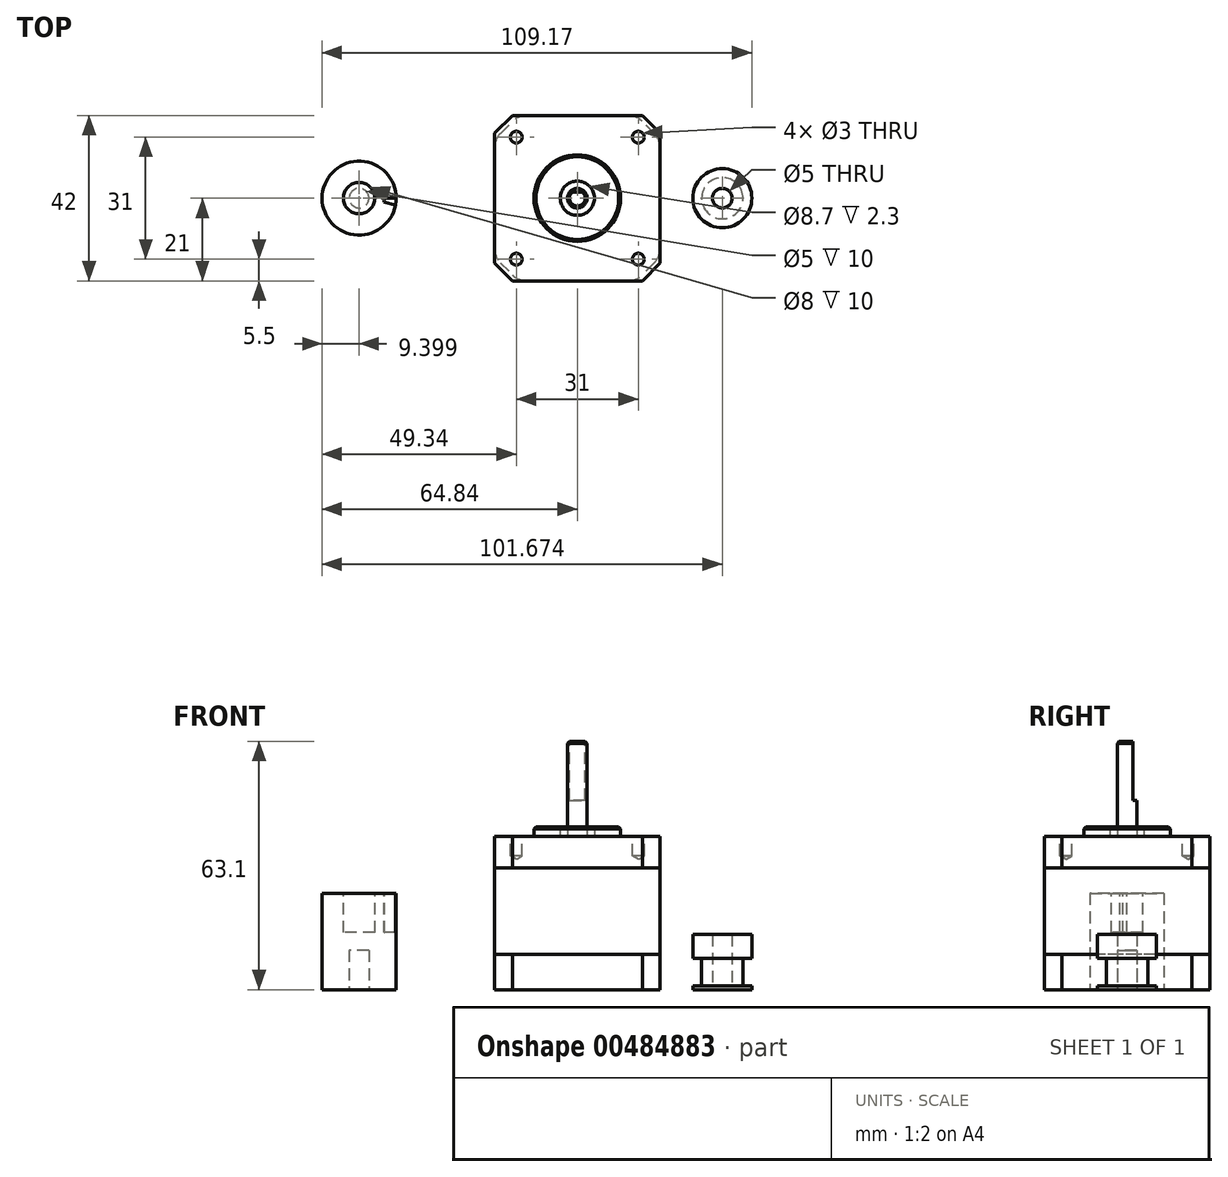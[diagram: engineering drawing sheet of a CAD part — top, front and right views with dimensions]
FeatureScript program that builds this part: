
annotation { "Feature Type Name" : "Feature", "Feature Type Description" : "" }
export const myFeature = defineFeature(function(context is Context, id is Id, definition is map)
    precondition{}
    {
        {
            var Q0;
            Q0=qCreatedBy(makeId("Top.planeOp"),FACE);
            var sketch = newSketch(context, id + "F0", { "sketchPlane" : qUnion([Q0])});
            skLineSegment(sketch, "E0.bottom", {"start": v(21, 21) * mm, "end": v(-21, 21) * mm});
            skLineSegment(sketch, "E0.top", {"start": v(21, -21) * mm, "end": v(-21, -21) * mm});
            skLineSegment(sketch, "E0.left", {"start": v(21, 21) * mm, "end": v(21, -21) * mm});
            skLineSegment(sketch, "E0.right", {"start": v(-21, 21) * mm, "end": v(-21, -21) * mm});
            skPoint(sketch, "E0.middle", {"position": v(0, 0) * mm});
            skSolve(sketch);
        }
        {
            var Q0;
            Q0=makeQuery(id+"F0.imprint","IMPRINT",FACE,{"disambiguationData":[TD([[makeQuery(id+"F0.imprint","IMPRINT",EDGE,{"derivedFrom":sQuery(id+"F0.wireOp",EDGE,"E0.bottom")}),1.0]])]});
            extrude(context, id + "F1", {"entities" : qUnion([Q0]), "depth" : 9 * mm, "offsetDistance" : 25 * mm});
        }
        {
            var Q0;
            Q0=makeQuery(id+"F1.opExtrude","SWEPT_EDGE",EDGE,{"disambiguationData":[OSD([sQuery(id+"F0.wireOp",EDGE,"E0.top"),sQuery(id+"F0.wireOp",EDGE,"E0.right")])]});
            var Q1;
            Q1=makeQuery(id+"F1.opExtrude","SWEPT_EDGE",EDGE,{"disambiguationData":[OSD([sQuery(id+"F0.wireOp",EDGE,"E0.top"),sQuery(id+"F0.wireOp",EDGE,"E0.left")])]});
            var Q2;
            Q2=makeQuery(id+"F1.opExtrude","SWEPT_EDGE",EDGE,{"disambiguationData":[OSD([sQuery(id+"F0.wireOp",EDGE,"E0.bottom"),sQuery(id+"F0.wireOp",EDGE,"E0.right")])]});
            var Q3;
            Q3=makeQuery(id+"F1.opExtrude","SWEPT_EDGE",EDGE,{"disambiguationData":[OSD([sQuery(id+"F0.wireOp",EDGE,"E0.bottom"),sQuery(id+"F0.wireOp",EDGE,"E0.left")])]});
            chamfer(context, id + "F2", {"entities" : qUnion([Q0, Q1, Q2, Q3]), "width" : 4.5 * mm, "tangentPropagation" : true});
        }
        {
            var Q0;
            Q0=makeQuery(id+"F1.opExtrude","CAP_FACE",FACE,{"disambiguationData":[OSD([sQuery(id+"F0.wireOp",EDGE,"E0.bottom"),sQuery(id+"F0.wireOp",EDGE,"E0.top"),sQuery(id+"F0.wireOp",EDGE,"E0.left"),sQuery(id+"F0.wireOp",EDGE,"E0.right")])],"isStart":false});
            var sketch = newSketch(context, id + "F3", { "sketchPlane" : qUnion([Q0])});
            skLineSegment(sketch, "E1.bottom", {"start": v(21, 21) * mm, "end": v(-21, 21) * mm});
            skLineSegment(sketch, "E1.top", {"start": v(21, -21) * mm, "end": v(-21, -21) * mm});
            skLineSegment(sketch, "E1.left", {"start": v(21, 21) * mm, "end": v(21, -21) * mm});
            skLineSegment(sketch, "E1.right", {"start": v(-21, 21) * mm, "end": v(-21, -21) * mm});
            skPoint(sketch, "E1.middle", {"position": v(0, 0) * mm});
            skSolve(sketch);
        }
        {
            var Q0;
            {var subQ1=sQuery(id+"F0.wireOp",EDGE,"E0.right");var subQ2=sQuery(id+"F0.wireOp",EDGE,"E0.left");var subQ3=sQuery(id+"F0.wireOp",EDGE,"E0.top");var subQ4=sQuery(id+"F0.wireOp",EDGE,"E0.bottom");var subQ5=makeQuery(id+"F1.opExtrude","CAP_FACE",FACE,{"disambiguationData":[OSD([subQ4,subQ3,subQ2,subQ1])],"isStart":false});var subQ9=makeQuery(id+"F2.opChamfer","BLEND_EDGE",EDGE,{"blendedFrom":[makeQuery(id+"F1.opExtrude","SWEPT_EDGE",EDGE,{"disambiguationData":[OSD([subQ4,subQ2])]}),subQ5],"blendedInto":[subQ5]});Q0=makeQuery(id+"F3.imprint","IMPRINT",FACE,{"disambiguationData":[TD([[makeQuery(id+"F3.imprint","IMPRINT",EDGE,{"derivedFrom":subQ9}),1.0]])]});}
            var Q1;
            {var subQ1=sQuery(id+"F0.wireOp",EDGE,"E0.right");var subQ2=sQuery(id+"F0.wireOp",EDGE,"E0.bottom");var subQ3=makeQuery(id+"F2.opChamfer","BLEND_EDGE",EDGE,{"blendedFrom":[makeQuery(id+"F1.opExtrude","SWEPT_EDGE",EDGE,{"disambiguationData":[OSD([subQ2,subQ1])]}),makeQuery(id+"F1.opExtrude","CAP_FACE",FACE,{"disambiguationData":[OSD([subQ2,sQuery(id+"F0.wireOp",EDGE,"E0.top"),sQuery(id+"F0.wireOp",EDGE,"E0.left"),subQ1])],"isStart":false})],"blendedInto":[makeQuery(id+"F1.opExtrude","CAP_FACE",FACE,{"disambiguationData":[OSD([subQ2,sQuery(id+"F0.wireOp",EDGE,"E0.top"),sQuery(id+"F0.wireOp",EDGE,"E0.left"),subQ1])],"isStart":false})]});Q1=makeQuery(id+"F3.imprint","IMPRINT",FACE,{"disambiguationData":[TD([[makeQuery(id+"F3.imprint","IMPRINT",EDGE,{"derivedFrom":subQ3}),-1.0]])]});}
            var Q2;
            {var subQ1=sQuery(id+"F0.wireOp",EDGE,"E0.left");var subQ2=sQuery(id+"F0.wireOp",EDGE,"E0.bottom");var subQ3=makeQuery(id+"F2.opChamfer","BLEND_EDGE",EDGE,{"blendedFrom":[makeQuery(id+"F1.opExtrude","SWEPT_EDGE",EDGE,{"disambiguationData":[OSD([subQ2,subQ1])]}),makeQuery(id+"F1.opExtrude","CAP_FACE",FACE,{"disambiguationData":[OSD([subQ2,sQuery(id+"F0.wireOp",EDGE,"E0.top"),subQ1,sQuery(id+"F0.wireOp",EDGE,"E0.right")])],"isStart":false})],"blendedInto":[makeQuery(id+"F1.opExtrude","CAP_FACE",FACE,{"disambiguationData":[OSD([subQ2,sQuery(id+"F0.wireOp",EDGE,"E0.top"),subQ1,sQuery(id+"F0.wireOp",EDGE,"E0.right")])],"isStart":false})]});Q2=makeQuery(id+"F3.imprint","IMPRINT",FACE,{"disambiguationData":[TD([[makeQuery(id+"F3.imprint","IMPRINT",EDGE,{"derivedFrom":subQ3}),-1.0]])]});}
            var Q3;
            {var subQ1=sQuery(id+"F0.wireOp",EDGE,"E0.right");var subQ2=sQuery(id+"F0.wireOp",EDGE,"E0.top");var subQ3=makeQuery(id+"F2.opChamfer","BLEND_EDGE",EDGE,{"blendedFrom":[makeQuery(id+"F1.opExtrude","SWEPT_EDGE",EDGE,{"disambiguationData":[OSD([subQ2,subQ1])]}),makeQuery(id+"F1.opExtrude","CAP_FACE",FACE,{"disambiguationData":[OSD([sQuery(id+"F0.wireOp",EDGE,"E0.bottom"),subQ2,sQuery(id+"F0.wireOp",EDGE,"E0.left"),subQ1])],"isStart":false})],"blendedInto":[makeQuery(id+"F1.opExtrude","CAP_FACE",FACE,{"disambiguationData":[OSD([sQuery(id+"F0.wireOp",EDGE,"E0.bottom"),subQ2,sQuery(id+"F0.wireOp",EDGE,"E0.left"),subQ1])],"isStart":false})]});Q3=makeQuery(id+"F3.imprint","IMPRINT",FACE,{"disambiguationData":[TD([[makeQuery(id+"F3.imprint","IMPRINT",EDGE,{"derivedFrom":subQ3}),-1.0]])]});}
            var Q4;
            {var subQ1=sQuery(id+"F0.wireOp",EDGE,"E0.left");var subQ2=sQuery(id+"F0.wireOp",EDGE,"E0.top");var subQ3=makeQuery(id+"F2.opChamfer","BLEND_EDGE",EDGE,{"blendedFrom":[makeQuery(id+"F1.opExtrude","SWEPT_EDGE",EDGE,{"disambiguationData":[OSD([subQ2,subQ1])]}),makeQuery(id+"F1.opExtrude","CAP_FACE",FACE,{"disambiguationData":[OSD([sQuery(id+"F0.wireOp",EDGE,"E0.bottom"),subQ2,subQ1,sQuery(id+"F0.wireOp",EDGE,"E0.right")])],"isStart":false})],"blendedInto":[makeQuery(id+"F1.opExtrude","CAP_FACE",FACE,{"disambiguationData":[OSD([sQuery(id+"F0.wireOp",EDGE,"E0.bottom"),subQ2,subQ1,sQuery(id+"F0.wireOp",EDGE,"E0.right")])],"isStart":false})]});Q4=makeQuery(id+"F3.imprint","IMPRINT",FACE,{"disambiguationData":[TD([[makeQuery(id+"F3.imprint","IMPRINT",EDGE,{"derivedFrom":subQ3}),-1.0]])]});}
            extrude(context, id + "F4", {"entities" : qUnion([Q0, Q1, Q2, Q3, Q4]), "depth" : 22 * mm, "offsetDistance" : 25 * mm});
        }
        {
            var Q0;
            Q0=makeQuery(id+"F4.opExtrude","SWEPT_EDGE",EDGE,{"disambiguationData":[OSD([sQuery(id+"F3.wireOp",EDGE,"E1.bottom"),sQuery(id+"F3.wireOp",EDGE,"E1.right")])]});
            var Q1;
            Q1=makeQuery(id+"F4.opExtrude","SWEPT_EDGE",EDGE,{"disambiguationData":[OSD([sQuery(id+"F3.wireOp",EDGE,"E1.top"),sQuery(id+"F3.wireOp",EDGE,"E1.right")])]});
            var Q2;
            Q2=makeQuery(id+"F4.opExtrude","SWEPT_EDGE",EDGE,{"disambiguationData":[OSD([sQuery(id+"F3.wireOp",EDGE,"E1.bottom"),sQuery(id+"F3.wireOp",EDGE,"E1.left")])]});
            var Q3;
            Q3=makeQuery(id+"F4.opExtrude","SWEPT_EDGE",EDGE,{"disambiguationData":[OSD([sQuery(id+"F3.wireOp",EDGE,"E1.top"),sQuery(id+"F3.wireOp",EDGE,"E1.left")])]});
            chamfer(context, id + "F5", {"entities" : qUnion([Q0, Q1, Q2, Q3]), "width" : 6 * mm, "tangentPropagation" : true});
        }
        {
            var Q0;
            {var subQ0=sQuery(id+"F3.wireOp",EDGE,"E1.bottom");Q0=makeQuery(id+"F5.opChamfer","BLEND_EDGE",EDGE,{"blendedFrom":[makeQuery(id+"F4.opExtrude","SWEPT_EDGE",EDGE,{"disambiguationData":[OSD([subQ0,sQuery(id+"F3.wireOp",EDGE,"E1.right")])]}),makeQuery(id+"F4.opExtrude","SWEPT_FACE",FACE,{"disambiguationData":[OSD([subQ0])]})],"blendedInto":[makeQuery(id+"F4.opExtrude","SWEPT_FACE",FACE,{"disambiguationData":[OSD([subQ0])]})]});}
            var Q1;
            {var subQ0=sQuery(id+"F3.wireOp",EDGE,"E1.right");Q1=makeQuery(id+"F5.opChamfer","BLEND_EDGE",EDGE,{"blendedFrom":[makeQuery(id+"F4.opExtrude","SWEPT_EDGE",EDGE,{"disambiguationData":[OSD([sQuery(id+"F3.wireOp",EDGE,"E1.bottom"),subQ0])]}),makeQuery(id+"F4.opExtrude","SWEPT_FACE",FACE,{"disambiguationData":[OSD([subQ0])]})],"blendedInto":[makeQuery(id+"F4.opExtrude","SWEPT_FACE",FACE,{"disambiguationData":[OSD([subQ0])]})]});}
            var Q2;
            {var subQ0=sQuery(id+"F3.wireOp",EDGE,"E1.right");Q2=makeQuery(id+"F5.opChamfer","BLEND_EDGE",EDGE,{"blendedFrom":[makeQuery(id+"F4.opExtrude","SWEPT_EDGE",EDGE,{"disambiguationData":[OSD([sQuery(id+"F3.wireOp",EDGE,"E1.top"),subQ0])]}),makeQuery(id+"F4.opExtrude","SWEPT_FACE",FACE,{"disambiguationData":[OSD([subQ0])]})],"blendedInto":[makeQuery(id+"F4.opExtrude","SWEPT_FACE",FACE,{"disambiguationData":[OSD([subQ0])]})]});}
            var Q3;
            {var subQ0=sQuery(id+"F3.wireOp",EDGE,"E1.top");Q3=makeQuery(id+"F5.opChamfer","BLEND_EDGE",EDGE,{"blendedFrom":[makeQuery(id+"F4.opExtrude","SWEPT_EDGE",EDGE,{"disambiguationData":[OSD([subQ0,sQuery(id+"F3.wireOp",EDGE,"E1.right")])]}),makeQuery(id+"F4.opExtrude","SWEPT_FACE",FACE,{"disambiguationData":[OSD([subQ0])]})],"blendedInto":[makeQuery(id+"F4.opExtrude","SWEPT_FACE",FACE,{"disambiguationData":[OSD([subQ0])]})]});}
            var Q4;
            {var subQ0=sQuery(id+"F3.wireOp",EDGE,"E1.top");Q4=makeQuery(id+"F5.opChamfer","BLEND_EDGE",EDGE,{"blendedFrom":[makeQuery(id+"F4.opExtrude","SWEPT_EDGE",EDGE,{"disambiguationData":[OSD([subQ0,sQuery(id+"F3.wireOp",EDGE,"E1.left")])]}),makeQuery(id+"F4.opExtrude","SWEPT_FACE",FACE,{"disambiguationData":[OSD([subQ0])]})],"blendedInto":[makeQuery(id+"F4.opExtrude","SWEPT_FACE",FACE,{"disambiguationData":[OSD([subQ0])]})]});}
            var Q5;
            {var subQ0=sQuery(id+"F3.wireOp",EDGE,"E1.left");Q5=makeQuery(id+"F5.opChamfer","BLEND_EDGE",EDGE,{"blendedFrom":[makeQuery(id+"F4.opExtrude","SWEPT_EDGE",EDGE,{"disambiguationData":[OSD([sQuery(id+"F3.wireOp",EDGE,"E1.top"),subQ0])]}),makeQuery(id+"F4.opExtrude","SWEPT_FACE",FACE,{"disambiguationData":[OSD([subQ0])]})],"blendedInto":[makeQuery(id+"F4.opExtrude","SWEPT_FACE",FACE,{"disambiguationData":[OSD([subQ0])]})]});}
            var Q6;
            {var subQ0=sQuery(id+"F3.wireOp",EDGE,"E1.left");Q6=makeQuery(id+"F5.opChamfer","BLEND_EDGE",EDGE,{"blendedFrom":[makeQuery(id+"F4.opExtrude","SWEPT_EDGE",EDGE,{"disambiguationData":[OSD([sQuery(id+"F3.wireOp",EDGE,"E1.bottom"),subQ0])]}),makeQuery(id+"F4.opExtrude","SWEPT_FACE",FACE,{"disambiguationData":[OSD([subQ0])]})],"blendedInto":[makeQuery(id+"F4.opExtrude","SWEPT_FACE",FACE,{"disambiguationData":[OSD([subQ0])]})]});}
            var Q7;
            {var subQ0=sQuery(id+"F3.wireOp",EDGE,"E1.bottom");Q7=makeQuery(id+"F5.opChamfer","BLEND_EDGE",EDGE,{"blendedFrom":[makeQuery(id+"F4.opExtrude","SWEPT_EDGE",EDGE,{"disambiguationData":[OSD([subQ0,sQuery(id+"F3.wireOp",EDGE,"E1.left")])]}),makeQuery(id+"F4.opExtrude","SWEPT_FACE",FACE,{"disambiguationData":[OSD([subQ0])]})],"blendedInto":[makeQuery(id+"F4.opExtrude","SWEPT_FACE",FACE,{"disambiguationData":[OSD([subQ0])]})]});}
            fillet(context, id + "F6", {"entities" : qUnion([Q0, Q1, Q2, Q3, Q4, Q5, Q6, Q7]), "radius" : 5 * mm, "tangentPropagation" : true, "allowEdgeOverflow" : false});
        }
        {
            var Q0;
            Q0=makeQuery(id+"F4.opExtrude","CAP_FACE",FACE,{"disambiguationData":[OSD([sQuery(id+"F3.wireOp",EDGE,"E1.bottom"),sQuery(id+"F3.wireOp",EDGE,"E1.top"),sQuery(id+"F3.wireOp",EDGE,"E1.left"),sQuery(id+"F3.wireOp",EDGE,"E1.right")])],"isStart":false});
            var sketch = newSketch(context, id + "F7", { "sketchPlane" : qUnion([Q0])});
            skLineSegment(sketch, "E2.bottom", {"start": v(-21, 21) * mm, "end": v(21, 21) * mm});
            skLineSegment(sketch, "E2.top", {"start": v(-21, -21) * mm, "end": v(21, -21) * mm});
            skLineSegment(sketch, "E2.left", {"start": v(-21, 21) * mm, "end": v(-21, -21) * mm});
            skLineSegment(sketch, "E2.right", {"start": v(21, 21) * mm, "end": v(21, -21) * mm});
            skPoint(sketch, "E2.middle", {"position": v(0, 0) * mm});
            skSolve(sketch);
        }
        {
            var Q0;
            {var subQ0=sQuery(id+"F3.wireOp",EDGE,"E1.right");var subQ1=sQuery(id+"F3.wireOp",EDGE,"E1.left");var subQ2=sQuery(id+"F3.wireOp",EDGE,"E1.top");var subQ3=sQuery(id+"F3.wireOp",EDGE,"E1.bottom");var subQ4=makeQuery(id+"F4.opExtrude","CAP_FACE",FACE,{"disambiguationData":[OSD([subQ3,subQ2,subQ1,subQ0])],"isStart":false});var subQ10=makeQuery(id+"F4.opExtrude","SWEPT_EDGE",EDGE,{"disambiguationData":[OSD([subQ3,subQ1])]});Q0=makeQuery(id+"F7.imprint","IMPRINT",FACE,{"disambiguationData":[TD([[makeQuery(id+"F7.imprint","IMPRINT",EDGE,{"derivedFrom":makeQuery(id+"F5.opChamfer","BLEND_EDGE",EDGE,{"blendedFrom":[subQ10,subQ4],"blendedInto":[subQ4]})}),1.0]])]});}
            var Q1;
            {var subQ0=sQuery(id+"F3.wireOp",EDGE,"E1.right");var subQ1=sQuery(id+"F3.wireOp",EDGE,"E1.bottom");var subQ2=makeQuery(id+"F4.opExtrude","CAP_FACE",FACE,{"disambiguationData":[OSD([subQ1,sQuery(id+"F3.wireOp",EDGE,"E1.top"),sQuery(id+"F3.wireOp",EDGE,"E1.left"),subQ0])],"isStart":false});var subQ3=makeQuery(id+"F4.opExtrude","SWEPT_EDGE",EDGE,{"disambiguationData":[OSD([subQ1,subQ0])]});Q1=makeQuery(id+"F7.imprint","IMPRINT",FACE,{"disambiguationData":[TD([[makeQuery(id+"F7.imprint","IMPRINT",EDGE,{"derivedFrom":makeQuery(id+"F5.opChamfer","BLEND_EDGE",EDGE,{"blendedFrom":[subQ3,subQ2],"blendedInto":[subQ2]})}),-1.0]])]});}
            var Q2;
            {var subQ0=sQuery(id+"F3.wireOp",EDGE,"E1.left");var subQ1=sQuery(id+"F3.wireOp",EDGE,"E1.bottom");var subQ2=makeQuery(id+"F4.opExtrude","CAP_FACE",FACE,{"disambiguationData":[OSD([subQ1,sQuery(id+"F3.wireOp",EDGE,"E1.top"),subQ0,sQuery(id+"F3.wireOp",EDGE,"E1.right")])],"isStart":false});var subQ3=makeQuery(id+"F4.opExtrude","SWEPT_EDGE",EDGE,{"disambiguationData":[OSD([subQ1,subQ0])]});Q2=makeQuery(id+"F7.imprint","IMPRINT",FACE,{"disambiguationData":[TD([[makeQuery(id+"F7.imprint","IMPRINT",EDGE,{"derivedFrom":makeQuery(id+"F5.opChamfer","BLEND_EDGE",EDGE,{"blendedFrom":[subQ3,subQ2],"blendedInto":[subQ2]})}),-1.0]])]});}
            var Q3;
            {var subQ0=sQuery(id+"F3.wireOp",EDGE,"E1.right");var subQ1=sQuery(id+"F3.wireOp",EDGE,"E1.top");var subQ2=makeQuery(id+"F4.opExtrude","CAP_FACE",FACE,{"disambiguationData":[OSD([sQuery(id+"F3.wireOp",EDGE,"E1.bottom"),subQ1,sQuery(id+"F3.wireOp",EDGE,"E1.left"),subQ0])],"isStart":false});var subQ4=makeQuery(id+"F4.opExtrude","SWEPT_EDGE",EDGE,{"disambiguationData":[OSD([subQ1,subQ0])]});Q3=makeQuery(id+"F7.imprint","IMPRINT",FACE,{"disambiguationData":[TD([[makeQuery(id+"F7.imprint","IMPRINT",EDGE,{"derivedFrom":makeQuery(id+"F5.opChamfer","BLEND_EDGE",EDGE,{"blendedFrom":[subQ4,subQ2],"blendedInto":[subQ2]})}),-1.0]])]});}
            var Q4;
            {var subQ0=sQuery(id+"F3.wireOp",EDGE,"E1.left");var subQ1=sQuery(id+"F3.wireOp",EDGE,"E1.top");var subQ2=makeQuery(id+"F4.opExtrude","CAP_FACE",FACE,{"disambiguationData":[OSD([sQuery(id+"F3.wireOp",EDGE,"E1.bottom"),subQ1,subQ0,sQuery(id+"F3.wireOp",EDGE,"E1.right")])],"isStart":false});var subQ4=makeQuery(id+"F4.opExtrude","SWEPT_EDGE",EDGE,{"disambiguationData":[OSD([subQ1,subQ0])]});Q4=makeQuery(id+"F7.imprint","IMPRINT",FACE,{"disambiguationData":[TD([[makeQuery(id+"F7.imprint","IMPRINT",EDGE,{"derivedFrom":makeQuery(id+"F5.opChamfer","BLEND_EDGE",EDGE,{"blendedFrom":[subQ4,subQ2],"blendedInto":[subQ2]})}),-1.0]])]});}
            extrude(context, id + "F8", {"entities" : qUnion([Q0, Q1, Q2, Q3, Q4]), "depth" : 8 * mm, "offsetDistance" : 25 * mm});
        }
        {
            var Q0;
            Q0=makeQuery(id+"F8.opExtrude","SWEPT_EDGE",EDGE,{"disambiguationData":[OSD([sQuery(id+"F7.wireOp",EDGE,"E2.bottom"),sQuery(id+"F7.wireOp",EDGE,"E2.left")])]});
            var Q1;
            Q1=makeQuery(id+"F8.opExtrude","SWEPT_EDGE",EDGE,{"disambiguationData":[OSD([sQuery(id+"F7.wireOp",EDGE,"E2.bottom"),sQuery(id+"F7.wireOp",EDGE,"E2.right")])]});
            var Q2;
            Q2=makeQuery(id+"F8.opExtrude","SWEPT_EDGE",EDGE,{"disambiguationData":[OSD([sQuery(id+"F7.wireOp",EDGE,"E2.top"),sQuery(id+"F7.wireOp",EDGE,"E2.left")])]});
            var Q3;
            Q3=makeQuery(id+"F8.opExtrude","SWEPT_EDGE",EDGE,{"disambiguationData":[OSD([sQuery(id+"F7.wireOp",EDGE,"E2.top"),sQuery(id+"F7.wireOp",EDGE,"E2.right")])]});
            chamfer(context, id + "F9", {"entities" : qUnion([Q0, Q1, Q2, Q3]), "width" : 4.5 * mm, "tangentPropagation" : true});
        }
        {
            var Q0;
            Q0=makeQuery(id+"F8.opExtrude","CAP_FACE",FACE,{"disambiguationData":[OSD([sQuery(id+"F7.wireOp",EDGE,"E2.bottom"),sQuery(id+"F7.wireOp",EDGE,"E2.top"),sQuery(id+"F7.wireOp",EDGE,"E2.left"),sQuery(id+"F7.wireOp",EDGE,"E2.right")])],"isStart":false});
            var sketch = newSketch(context, id + "F10", { "sketchPlane" : qUnion([Q0])});
            skCircle(sketch, "E3", {"center": v(0, 0) * mm, "radius": 11 * mm});
            skCircle(sketch, "E4", {"center": v(0, 0) * mm, "radius": 4.35 * mm});
            skCircle(sketch, "E5", {"center": v(0, 0) * mm, "radius": 2.5 * mm});
            skLineSegment(sketch, "E6", {"start": v(-21, 15.5) * mm, "end": v(-15.5, 15.5) * mm, "construction": true});
            skLineSegment(sketch, "E7", {"start": v(-15.5, 15.5) * mm, "end": v(15.5, 15.5) * mm, "construction": true});
            skLineSegment(sketch, "E8", {"start": v(15.5, 15.5) * mm, "end": v(21, 15.5) * mm, "construction": true});
            skLineSegment(sketch, "E9", {"start": v(-21, -15.5) * mm, "end": v(-15.5, -15.5) * mm, "construction": true});
            skLineSegment(sketch, "E10", {"start": v(-15.5, -15.5) * mm, "end": v(15.5, -15.5) * mm, "construction": true});
            skLineSegment(sketch, "E11", {"start": v(15.5, -15.5) * mm, "end": v(21, -15.5) * mm, "construction": true});
            skLineSegment(sketch, "E12", {"start": v(-15.5, 15.5) * mm, "end": v(-15.5, -15.5) * mm, "construction": true});
            skLineSegment(sketch, "E13", {"start": v(0, -15.5) * mm, "end": v(0, -21) * mm});
            skLineSegment(sketch, "E14", {"start": v(0, 15.5) * mm, "end": v(0, 21) * mm});
            skSolve(sketch);
        }
        {
            var Q0;
            Q0=makeQuery(id+"F10.imprint","IMPRINT",FACE,{"disambiguationData":[TD([[makeQuery(id+"F10.imprint","IMPRINT",EDGE,{"derivedFrom":sQuery(id+"F10.wireOp",EDGE,"E3")}),1.0]])]});
            extrude(context, id + "F11", {"entities" : qUnion([Q0]), "operationType" : NewBodyOperationType.ADD, "depth" : 2.3 * mm, "offsetDistance" : 25 * mm});
        }
        {
            var Q0;
            Q0=makeQuery(id+"F10.imprint","IMPRINT",FACE,{"disambiguationData":[TD([[makeQuery(id+"F10.imprint","IMPRINT",EDGE,{"derivedFrom":sQuery(id+"F10.wireOp",EDGE,"E5")}),1.0]])]});
            extrude(context, id + "F12", {"entities" : qUnion([Q0]), "depth" : 24.1 * mm, "offsetDistance" : 25 * mm});
        }
        {
            var Q0;
            Q0=makeQuery(id+"F12.opExtrude","CAP_FACE",FACE,{"disambiguationData":[OSD([sQuery(id+"F10.wireOp",EDGE,"E5")])],"isStart":false});
            var sketch = newSketch(context, id + "F13", { "sketchPlane" : qUnion([Q0])});
            skLineSegment(sketch, "E15", {"start": v(-2, 1.5) * mm, "end": v(2, 1.5) * mm});
            skSolve(sketch);
        }
        {
            var Q0;
            {var subQ0=sQuery(id+"F13.wireOp",EDGE,"E15");Q0=makeQuery(id+"F13.imprint","IMPRINT",FACE,{"disambiguationData":[TD([[makeQuery(id+"F13.imprint","IMPRINT",EDGE,{"derivedFrom":subQ0}),1.0]])]});}
            extrude(context, id + "F14", {"entities" : qUnion([Q0]), "operationType" : NewBodyOperationType.REMOVE, "oppositeDirection" : true, "depth" : 15 * mm, "offsetDistance" : 25 * mm});
        }
        {
            var Q0;
            Q0=makeQuery(id+"F12.opExtrude","CAP_EDGE",EDGE,{"disambiguationData":[OSD([sQuery(id+"F10.wireOp",EDGE,"E5")])],"isStart":false});
            chamfer(context, id + "F15", {"entities" : qUnion([Q0]), "width" : 0.5 * mm, "tangentPropagation" : true});
        }
        {
            var Q0;
            Q0=makeQuery(id+"F11.opExtrude","CAP_EDGE",EDGE,{"disambiguationData":[OSD([sQuery(id+"F10.wireOp",EDGE,"E3")])],"isStart":false});
            chamfer(context, id + "F16", {"entities" : qUnion([Q0]), "width" : 0.5 * mm, "tangentPropagation" : true});
        }
        {
            var Q0;
            Q0=sQuery(id+"F10.wireOp",VERTEX,"E12.start");
            var Q1;
            Q1=sQuery(id+"F10.wireOp",VERTEX,"E8.start");
            var Q2;
            Q2=sQuery(id+"F10.wireOp",VERTEX,"E11.start");
            var Q3;
            Q3=sQuery(id+"F10.wireOp",VERTEX,"E10.start");
            var Q4;
            Q4=makeQuery(id+"F8.opExtrude","SWEPT_BODY",BODY,{"disambiguationData":[OSD([sQuery(id+"F7.wireOp",EDGE,"E2.bottom"),sQuery(id+"F7.wireOp",EDGE,"E2.top"),sQuery(id+"F7.wireOp",EDGE,"E2.left"),sQuery(id+"F7.wireOp",EDGE,"E2.right")])]});
            hole(context, id + "F17", {"style" : HoleStyle.SIMPLE, "endStyle" : HoleEndStyle.BLIND, "holeDiameter" : 3 * mm, "majorDiameter" : 5 * mm, "holeDepth" : 5 * mm, "isTappedThrough" : true, "tappedDepth" : 12 * mm, "tapClearance" : 3, "locations" : qUnion([Q0, Q1, Q2, Q3]), "scope" : qUnion([Q4])});
        }
        {
            var Q0;
            Q0=qCreatedBy(makeId("Top.planeOp"),FACE);
            var sketch = newSketch(context, id + "F18", { "sketchPlane" : qUnion([Q0])});
            skCircle(sketch, "E16", {"center": v(-55.44, 0) * mm, "radius": 2.5 * mm});
            skCircle(sketch, "E17", {"center": v(-55.44, 0) * mm, "radius": 9.4 * mm});
            skSolve(sketch);
        }
        {
            var Q0;
            Q0 = qSketchRegion(id + "F18", true);
            var Q1;
            Q1=makeQuery(id+"F18.imprint","IMPRINT",FACE,{"disambiguationData":[TD([[makeQuery(id+"F18.imprint","IMPRINT",EDGE,{"derivedFrom":sQuery(id+"F18.wireOp",EDGE,"E16")}),1.0]])]});
            extrude(context, id + "F19", {"entities" : qUnion([Q0, Q1]), "depth" : 24.5 * mm, "offsetDistance" : 25 * mm});
        }
        {
            var Q0;
            Q0=makeQuery(id+"F18.imprint","IMPRINT",FACE,{"disambiguationData":[TD([[makeQuery(id+"F18.imprint","IMPRINT",EDGE,{"derivedFrom":sQuery(id+"F18.wireOp",EDGE,"E16")}),1.0]])]});
            extrude(context, id + "F20", {"entities" : qUnion([Q0]), "operationType" : NewBodyOperationType.REMOVE, "depth" : 10 * mm, "offsetDistance" : 25 * mm});
        }
        {
            var Q0;
            Q0=makeQuery(id+"F19.opExtrude","CAP_FACE",FACE,{"disambiguationData":[OSD([sQuery(id+"F18.wireOp",EDGE,"E17")])],"isStart":false});
            var sketch = newSketch(context, id + "F21", { "sketchPlane" : qUnion([Q0])});
            skCircle(sketch, "E18", {"center": v(-55.44, 0) * mm, "radius": 4 * mm});
            skLineSegment(sketch, "E19", {"start": v(-46.04, 0) * mm, "end": v(-49, 0) * mm});
            skLineSegment(sketch, "E20", {"start": v(-46.21, -1.78) * mm, "end": v(-49.14, -1) * mm});
            skLineSegment(sketch, "E21", {"start": v(-49.14, -1) * mm, "end": v(-49, 0) * mm});
            skSolve(sketch);
        }
        {
            var Q0;
            Q0=makeQuery(id+"F21.imprint","IMPRINT",FACE,{"disambiguationData":[TD([[makeQuery(id+"F21.imprint","IMPRINT",EDGE,{"derivedFrom":sQuery(id+"F21.wireOp",EDGE,"E18")}),1.0]])]});
            var Q1;
            {var subQ0=sQuery(id+"F21.wireOp",EDGE,"E19");Q1=makeQuery(id+"F21.imprint","IMPRINT",FACE,{"disambiguationData":[TD([[makeQuery(id+"F21.imprint","IMPRINT",EDGE,{"derivedFrom":subQ0}),1.0]])]});}
            extrude(context, id + "F22", {"entities" : qUnion([Q0, Q1]), "operationType" : NewBodyOperationType.REMOVE, "oppositeDirection" : true, "depth" : 10 * mm, "offsetDistance" : 25 * mm});
        }
        {
            var Q0;
            Q0=qCreatedBy(makeId("Top.planeOp"),FACE);
            var sketch = newSketch(context, id + "F23", { "sketchPlane" : qUnion([Q0])});
            skCircle(sketch, "E22", {"center": v(36.83, 0) * mm, "radius": 7.5 * mm});
            skCircle(sketch, "E23", {"center": v(36.83, 0) * mm, "radius": 5.25 * mm});
            skCircle(sketch, "E24", {"center": v(36.83, 0) * mm, "radius": 2.5 * mm});
            skSolve(sketch);
        }
        {
            var Q0;
            Q0=makeQuery(id+"F23.imprint","IMPRINT",FACE,{"disambiguationData":[TD([[makeQuery(id+"F23.imprint","IMPRINT",EDGE,{"derivedFrom":sQuery(id+"F23.wireOp",EDGE,"E22")}),1.0]])]});
            extrude(context, id + "F24", {"entities" : qUnion([Q0]), "depth" : 1 * mm, "offsetDistance" : 25 * mm});
        }
        {
            var Q0;
            Q0=makeQuery(id+"F23.imprint","IMPRINT",FACE,{"disambiguationData":[TD([[makeQuery(id+"F23.imprint","IMPRINT",EDGE,{"derivedFrom":sQuery(id+"F23.wireOp",EDGE,"E23")}),1.0]])]});
            var Q1;
            Q1=makeQuery(id+"F23.imprint","IMPRINT",FACE,{"disambiguationData":[TD([[makeQuery(id+"F23.imprint","IMPRINT",EDGE,{"derivedFrom":sQuery(id+"F23.wireOp",EDGE,"E24")}),1.0]])]});
            extrude(context, id + "F25", {"entities" : qUnion([Q0, Q1]), "operationType" : NewBodyOperationType.ADD, "depth" : 8 * mm, "offsetDistance" : 25 * mm});
        }
        {
            var Q0;
            Q0=makeQuery(id+"F25.opExtrude","CAP_FACE",FACE,{"disambiguationData":[OSD([sQuery(id+"F23.wireOp",EDGE,"E23")])],"isStart":false});
            var sketch = newSketch(context, id + "F26", { "sketchPlane" : qUnion([Q0])});
            skCircle(sketch, "E25", {"center": v(36.83, 0) * mm, "radius": 7.5 * mm});
            skSolve(sketch);
        }
        {
            var Q0;
            Q0=makeQuery(id+"F26.imprint","IMPRINT",FACE,{"disambiguationData":[TD([[makeQuery(id+"F26.imprint","IMPRINT",EDGE,{"derivedFrom":makeQuery(id+"F25.opExtrude","CAP_EDGE",EDGE,{"disambiguationData":[OSD([sQuery(id+"F23.wireOp",EDGE,"E23")])],"isStart":false})}),1.0]])]});
            var Q1;
            Q1=makeQuery(id+"F26.imprint","IMPRINT",FACE,{"disambiguationData":[TD([[makeQuery(id+"F26.imprint","IMPRINT",EDGE,{"derivedFrom":sQuery(id+"F26.wireOp",EDGE,"E25")}),1.0]])]});
            extrude(context, id + "F27", {"entities" : qUnion([Q0, Q1]), "operationType" : NewBodyOperationType.ADD, "depth" : 6 * mm, "offsetDistance" : 25 * mm});
        }
        {
            var Q0;
            Q0=makeQuery(id+"F23.imprint","IMPRINT",FACE,{"disambiguationData":[TD([[makeQuery(id+"F23.imprint","IMPRINT",EDGE,{"derivedFrom":sQuery(id+"F23.wireOp",EDGE,"E24")}),1.0]])]});
            extrude(context, id + "F28", {"entities" : qUnion([Q0]), "operationType" : NewBodyOperationType.REMOVE, "endBound" : BoundingType.UP_TO_NEXT, "depth" : 25 * mm, "offsetDistance" : 25 * mm});
        }
    });
